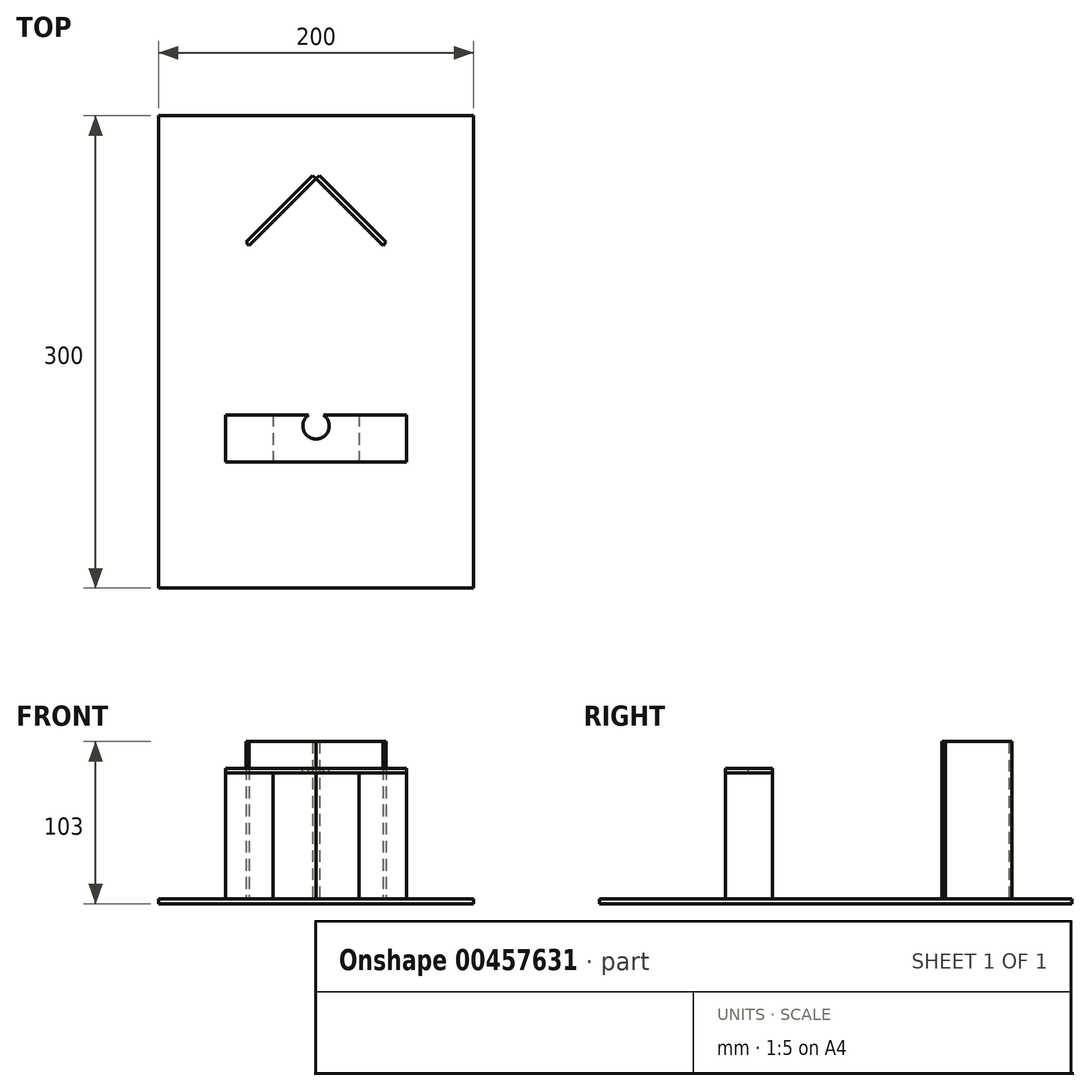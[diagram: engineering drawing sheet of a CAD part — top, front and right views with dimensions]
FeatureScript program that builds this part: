
annotation { "Feature Type Name" : "Feature", "Feature Type Description" : "" }
export const myFeature = defineFeature(function(context is Context, id is Id, definition is map)
    precondition{}
    {
        {
            var Q0;
            Q0=qCreatedBy(makeId("Top.planeOp"),FACE);
            var sketch = newSketch(context, id + "F0", { "sketchPlane" : qUnion([Q0])});
            skLineSegment(sketch, "E0.bottom", {"start": v(-100, 150) * mm, "end": v(100, 150) * mm});
            skLineSegment(sketch, "E0.top", {"start": v(-100, -150) * mm, "end": v(100, -150) * mm});
            skLineSegment(sketch, "E0.left", {"start": v(-100, 150) * mm, "end": v(-100, -150) * mm});
            skLineSegment(sketch, "E0.right", {"start": v(100, 150) * mm, "end": v(100, -150) * mm});
            skPoint(sketch, "E0.middle", {"position": v(0, 0) * mm});
            skLineSegment(sketch, "E1", {"start": v(0, 150) * mm, "end": v(0, -150) * mm, "construction": true});
            skLineSegment(sketch, "E2", {"start": v(0, 110) * mm, "end": v(-42.43, 67.57) * mm});
            skLineSegment(sketch, "E3", {"start": v(-42.43, 67.57) * mm, "end": v(-44.55, 69.7) * mm});
            skLineSegment(sketch, "E4", {"start": v(-44.55, 69.7) * mm, "end": v(-2.12, 112.12) * mm});
            skLineSegment(sketch, "E5", {"start": v(0, 110) * mm, "end": v(-2.12, 112.12) * mm});
            skLineSegment(sketch, "E6.MirrorCS", {"start": v(0, 110) * mm, "end": v(42.43, 67.57) * mm});
            skLineSegment(sketch, "E7.MirrorCS", {"start": v(44.55, 69.7) * mm, "end": v(2.12, 112.12) * mm});
            skLineSegment(sketch, "E8.MirrorCS", {"start": v(0, 110) * mm, "end": v(2.12, 112.12) * mm});
            skLineSegment(sketch, "E9.bottom", {"start": v(-57.43, -40) * mm, "end": v(-27.43, -40) * mm});
            skLineSegment(sketch, "E9.top", {"start": v(-57.43, -70) * mm, "end": v(-27.43, -70) * mm});
            skLineSegment(sketch, "E9.left", {"start": v(-57.43, -40) * mm, "end": v(-57.43, -70) * mm});
            skLineSegment(sketch, "E9.right", {"start": v(-27.43, -40) * mm, "end": v(-27.43, -70) * mm});
            skPoint(sketch, "E9.middle", {"position": v(-42.43, -55) * mm});
            skLineSegment(sketch, "E10", {"start": v(-42.43, 67.57) * mm, "end": v(-42.43, -150) * mm, "construction": true});
            skLineSegment(sketch, "E11.MirrorCS", {"start": v(57.43, -40) * mm, "end": v(27.43, -40) * mm});
            skLineSegment(sketch, "E12.MirrorCS", {"start": v(27.43, -40) * mm, "end": v(27.43, -70) * mm});
            skLineSegment(sketch, "E13.MirrorCS", {"start": v(57.43, -70) * mm, "end": v(27.43, -70) * mm});
            skLineSegment(sketch, "E14.MirrorCS", {"start": v(57.43, -40) * mm, "end": v(57.43, -70) * mm});
            skLineSegment(sketch, "E15.MirrorCS", {"start": v(42.43, 67.57) * mm, "end": v(44.55, 69.7) * mm});
            skSolve(sketch);
        }
        {
            var Q0;
            Q0=qCreatedBy(makeId("Top.planeOp"),FACE);
            var sketch = newSketch(context, id + "F1", { "sketchPlane" : qUnion([Q0])});
            skLineSegment(sketch, "E16.0", {"start": v(-100, 150) * mm, "end": v(-100, -150) * mm});
            skLineSegment(sketch, "E16.1", {"start": v(-100, 150) * mm, "end": v(100, 150) * mm});
            skLineSegment(sketch, "E16.2", {"start": v(100, 150) * mm, "end": v(100, -150) * mm});
            skLineSegment(sketch, "E16.3", {"start": v(-100, -150) * mm, "end": v(100, -150) * mm});
            skSolve(sketch);
        }
        {
            var Q0;
            Q0=makeQuery(id+"F1.imprint","IMPRINT",FACE,{"disambiguationData":[TD([[makeQuery(id+"F1.imprint","IMPRINT",EDGE,{"derivedFrom":sQuery(id+"F1.wireOp",EDGE,"E16.0")}),1.0]])]});
            extrude(context, id + "F2", {"entities" : qUnion([Q0]), "oppositeDirection" : true, "depth" : 3 * mm});
        }
        {
            var Q0;
            Q0=makeQuery(id+"F0.imprint","IMPRINT",FACE,{"disambiguationData":[TD([[makeQuery(id+"F0.imprint","IMPRINT",EDGE,{"derivedFrom":sQuery(id+"F0.wireOp",EDGE,"E9.bottom")}),-1.0]])]});
            var Q1;
            Q1=makeQuery(id+"F0.imprint","IMPRINT",FACE,{"disambiguationData":[TD([[makeQuery(id+"F0.imprint","IMPRINT",EDGE,{"derivedFrom":sQuery(id+"F0.wireOp",EDGE,"E11.MirrorCS")}),1.0]])]});
            extrude(context, id + "F3", {"entities" : qUnion([Q0, Q1]), "depth" : 80 * mm});
        }
        {
            var Q0;
            Q0=makeQuery(id+"F0.imprint","IMPRINT",FACE,{"disambiguationData":[TD([[makeQuery(id+"F0.imprint","IMPRINT",EDGE,{"derivedFrom":sQuery(id+"F0.wireOp",EDGE,"E2")}),-1.0]])]});
            var Q1;
            Q1=makeQuery(id+"F0.imprint","IMPRINT",FACE,{"disambiguationData":[TD([[makeQuery(id+"F0.imprint","IMPRINT",EDGE,{"derivedFrom":sQuery(id+"F0.wireOp",EDGE,"E6.MirrorCS")}),1.0]])]});
            extrude(context, id + "F4", {"entities" : qUnion([Q0, Q1]), "depth" : 100 * mm});
        }
        {
            var Q0;
            Q0=makeQuery(id+"F3.opExtrude","CAP_FACE",FACE,{"disambiguationData":[OSD([sQuery(id+"F0.wireOp",EDGE,"E9.bottom"),sQuery(id+"F0.wireOp",EDGE,"E9.top"),sQuery(id+"F0.wireOp",EDGE,"E9.left"),sQuery(id+"F0.wireOp",EDGE,"E9.right")])],"isStart":false});
            var sketch = newSketch(context, id + "F5", { "sketchPlane" : qUnion([Q0])});
            skLineSegment(sketch, "E17.0", {"start": v(-57.43, -70) * mm, "end": v(-27.43, -70) * mm});
            skLineSegment(sketch, "E17.1", {"start": v(57.43, -70) * mm, "end": v(27.43, -70) * mm});
            skLineSegment(sketch, "E17.2", {"start": v(-57.43, -40) * mm, "end": v(-27.43, -40) * mm});
            skLineSegment(sketch, "E17.3", {"start": v(57.43, -40) * mm, "end": v(27.43, -40) * mm});
            skLineSegment(sketch, "E18", {"start": v(-27.43, -70) * mm, "end": v(27.43, -70) * mm});
            skLineSegment(sketch, "E19", {"start": v(-27.43, -40) * mm, "end": v(27.43, -40) * mm});
            skLineSegment(sketch, "E20", {"start": v(-57.43, -70) * mm, "end": v(-57.43, -40) * mm});
            skLineSegment(sketch, "E21", {"start": v(57.43, -70) * mm, "end": v(57.43, -40) * mm});
            skSolve(sketch);
        }
        {
            var Q0;
            Q0=makeQuery(id+"F5.imprint","IMPRINT",FACE,{"disambiguationData":[TD([[makeQuery(id+"F5.imprint","IMPRINT",EDGE,{"derivedFrom":sQuery(id+"F5.wireOp",EDGE,"E17.0")}),1.0]])]});
            var Q1;
            Q1=makeQuery(id+"F5.imprint","IMPRINT",FACE,{"disambiguationData":[TD([[makeQuery(id+"F5.imprint","IMPRINT",EDGE,{"derivedFrom":sQuery(id+"F5.wireOp",EDGE,"E17.1")}),-1.0]])]});
            extrude(context, id + "F6", {"entities" : qUnion([Q0, Q1]), "depth" : 3 * mm});
        }
        {
            var Q0;
            Q0=makeQuery(id+"F6.opExtrude","CAP_FACE",FACE,{"disambiguationData":[OSD([sQuery(id+"F5.wireOp",EDGE,"E17.0"),sQuery(id+"F5.wireOp",EDGE,"E17.1"),sQuery(id+"F5.wireOp",EDGE,"E17.2"),sQuery(id+"F5.wireOp",EDGE,"E17.3"),sQuery(id+"F5.wireOp",EDGE,"E18"),sQuery(id+"F5.wireOp",EDGE,"E19"),sQuery(id+"F5.wireOp",EDGE,"E20"),sQuery(id+"F5.wireOp",EDGE,"E21")])],"isStart":false});
            var sketch = newSketch(context, id + "F7", { "sketchPlane" : qUnion([Q0])});
            skLineSegment(sketch, "E22.0", {"start": v(-57.43, -40) * mm, "end": v(57.43, -40) * mm, "construction": true});
            skLineSegment(sketch, "E23", {"start": v(0, -40) * mm, "end": v(0, -70) * mm, "construction": true});
            skCircle(sketch, "E24", {"center": v(0, -47) * mm, "radius": 8.4 * mm});
            skSolve(sketch);
        }
        {
            var Q0;
            {var subQ0=sQuery(id+"F7.wireOp",EDGE,"E24");var subQ1=makeQuery(id+"F6.opExtrude","CAP_EDGE",EDGE,{"disambiguationData":[OSD([sQuery(id+"F5.wireOp",EDGE,"E17.2"),sQuery(id+"F5.wireOp",EDGE,"E17.3"),sQuery(id+"F5.wireOp",EDGE,"E19")])],"isStart":false});var subQ2=makeQuery(id+"F7.imprint","INTERSECT",VERTEX,{"disambiguationData":[OD(0.0)],"derivedFrom":[subQ1,subQ0]});Q0=makeQuery(id+"F7.imprint","IMPRINT",FACE,{"disambiguationData":[TD([[makeQuery(id+"F7.imprint","IMPRINT",EDGE,{"disambiguationData":[TD([[subQ2,-1.0]])],"derivedFrom":subQ0}),1.0]])]});}
            extrude(context, id + "F8", {"entities" : qUnion([Q0]), "operationType" : NewBodyOperationType.REMOVE, "oppositeDirection" : true, "depth" : 25 * mm});
        }
    });
